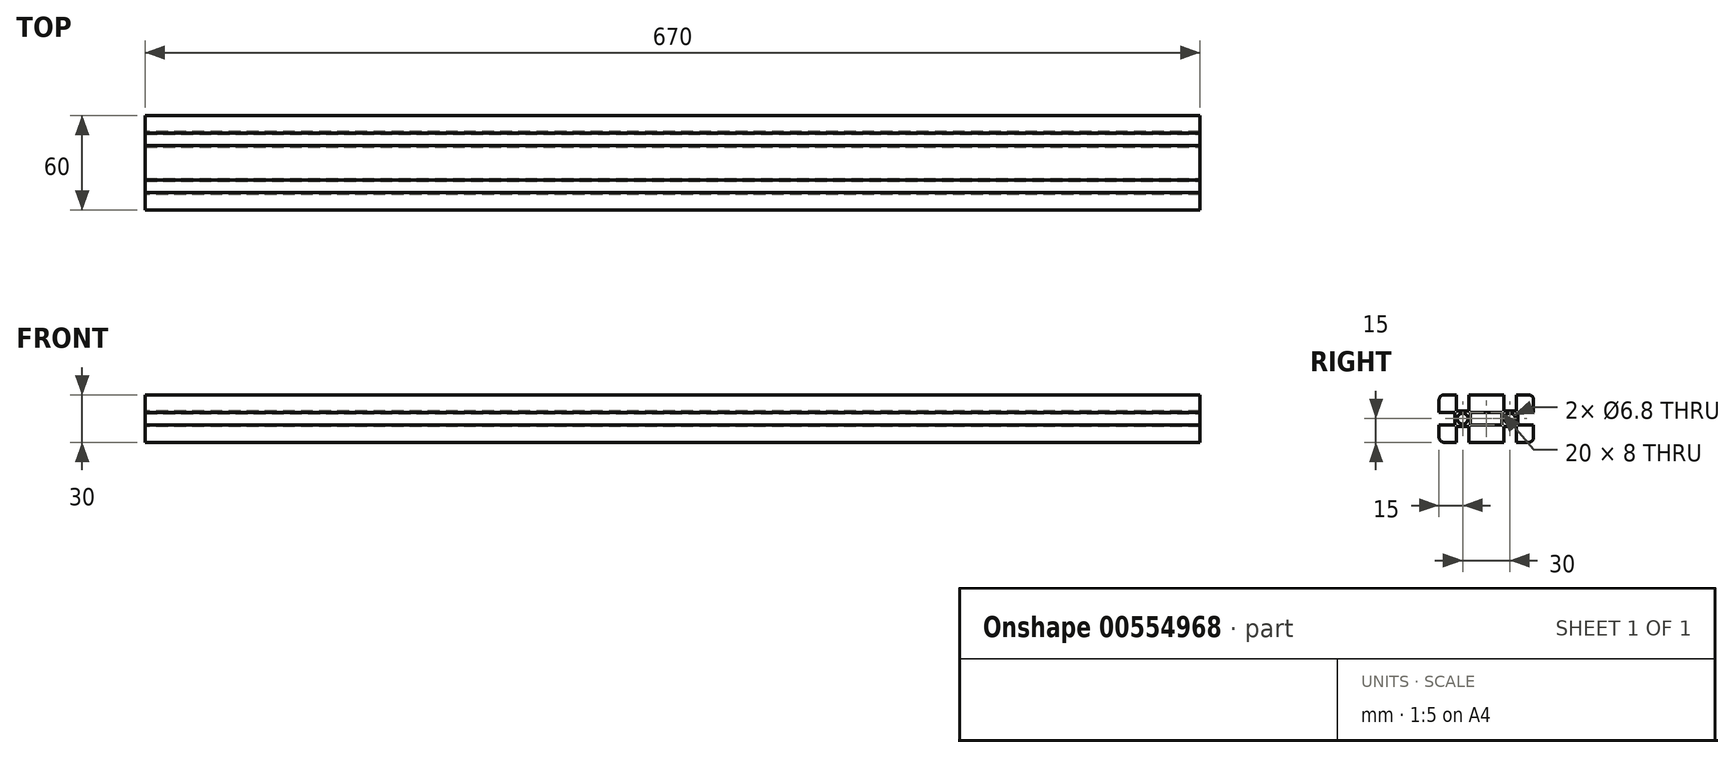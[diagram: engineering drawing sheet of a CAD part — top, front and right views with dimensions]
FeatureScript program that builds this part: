
annotation { "Feature Type Name" : "Feature", "Feature Type Description" : "" }
export const myFeature = defineFeature(function(context is Context, id is Id, definition is map)
    precondition{}
    {
        {
            var Q0;
            Q0=qCreatedBy(makeId("Right.planeOp"),FACE);
            var sketch = newSketch(context, id + "F0", { "sketchPlane" : qUnion([Q0])});
            skLineSegment(sketch, "E0.bottom", {"start": v(30, 15) * mm, "end": v(19, 15) * mm});
            skLineSegment(sketch, "E0.top", {"start": v(30, -15) * mm, "end": v(19, -15) * mm});
            skLineSegment(sketch, "E0.left", {"start": v(30, 15) * mm, "end": v(30, 4) * mm});
            skLineSegment(sketch, "E0.right", {"start": v(-30, 15) * mm, "end": v(-30, 4) * mm});
            skPoint(sketch, "E0.middle", {"position": v(0, 0) * mm});
            skLineSegment(sketch, "E1", {"start": v(-30, 4) * mm, "end": v(-20, 4) * mm});
            skLineSegment(sketch, "E2", {"start": v(-20, 4) * mm, "end": v(-20, -4) * mm});
            skLineSegment(sketch, "E3", {"start": v(-20, -4) * mm, "end": v(-30, -4) * mm});
            skLineSegment(sketch, "E4", {"start": v(-19, 15) * mm, "end": v(-19, 5) * mm});
            skLineSegment(sketch, "E5", {"start": v(-19, 5) * mm, "end": v(-11, 5) * mm});
            skLineSegment(sketch, "E6", {"start": v(-11, 5) * mm, "end": v(-11, 15) * mm});
            skLineSegment(sketch, "E7", {"start": v(-19, -15) * mm, "end": v(-19, -5) * mm});
            skLineSegment(sketch, "E8", {"start": v(-19, -5) * mm, "end": v(-11, -5) * mm});
            skLineSegment(sketch, "E9", {"start": v(-11, -5) * mm, "end": v(-11, -15) * mm});
            skLineSegment(sketch, "E10.MirrorCS", {"start": v(11, 5) * mm, "end": v(11, 15) * mm});
            skLineSegment(sketch, "E11.MirrorCS", {"start": v(20, 4) * mm, "end": v(20, -4) * mm});
            skLineSegment(sketch, "E12.MirrorCS", {"start": v(19, -5) * mm, "end": v(11, -5) * mm});
            skLineSegment(sketch, "E13.MirrorCS", {"start": v(11, -5) * mm, "end": v(11, -15) * mm});
            skLineSegment(sketch, "E14.MirrorCS", {"start": v(19, -15) * mm, "end": v(19, -5) * mm});
            skLineSegment(sketch, "E15.MirrorCS", {"start": v(20, -4) * mm, "end": v(30, -4) * mm});
            skLineSegment(sketch, "E16.MirrorCS", {"start": v(30, 4) * mm, "end": v(20, 4) * mm});
            skLineSegment(sketch, "E17.MirrorCS", {"start": v(19, 5) * mm, "end": v(11, 5) * mm});
            skLineSegment(sketch, "E18.MirrorCS", {"start": v(19, 15) * mm, "end": v(19, 5) * mm});
            skLineSegment(sketch, "E19.trimOffspring", {"start": v(-19, 15) * mm, "end": v(-30, 15) * mm});
            skLineSegment(sketch, "E20.trimOffspring", {"start": v(-30, -4) * mm, "end": v(-30, -15) * mm});
            skLineSegment(sketch, "E21.trimOffspring", {"start": v(-19, -15) * mm, "end": v(-30, -15) * mm});
            skLineSegment(sketch, "E22.trimOffspring", {"start": v(30, -4) * mm, "end": v(30, -15) * mm});
            skLineSegment(sketch, "E23.trimOffspring", {"start": v(11, 15) * mm, "end": v(-11, 15) * mm});
            skLineSegment(sketch, "E24.trimOffspring", {"start": v(11, -15) * mm, "end": v(-11, -15) * mm});
            skSolve(sketch);
        }
        {
            var Q0;
            Q0 = qSketchRegion(id + "F0", true);
            extrude(context, id + "F1", {"entities" : qUnion([Q0]), "endBound" : BoundingType.SYMMETRIC, "depth" : 670 * mm, "offsetDistance" : 25 * mm});
        }
        {
            var Q0;
            Q0=makeQuery(id+"F1.opExtrude","CAP_FACE",FACE,{"disambiguationData":[OSD([sQuery(id+"F0.wireOp",EDGE,"E0.bottom"),sQuery(id+"F0.wireOp",EDGE,"E0.top"),sQuery(id+"F0.wireOp",EDGE,"E0.left"),sQuery(id+"F0.wireOp",EDGE,"E0.right"),sQuery(id+"F0.wireOp",EDGE,"E1"),sQuery(id+"F0.wireOp",EDGE,"E2"),sQuery(id+"F0.wireOp",EDGE,"E3"),sQuery(id+"F0.wireOp",EDGE,"E4"),sQuery(id+"F0.wireOp",EDGE,"E5"),sQuery(id+"F0.wireOp",EDGE,"E6"),sQuery(id+"F0.wireOp",EDGE,"E7"),sQuery(id+"F0.wireOp",EDGE,"E8"),sQuery(id+"F0.wireOp",EDGE,"E9"),sQuery(id+"F0.wireOp",EDGE,"E10.MirrorCS"),sQuery(id+"F0.wireOp",EDGE,"E11.MirrorCS"),sQuery(id+"F0.wireOp",EDGE,"E12.MirrorCS"),sQuery(id+"F0.wireOp",EDGE,"E13.MirrorCS"),sQuery(id+"F0.wireOp",EDGE,"E14.MirrorCS"),sQuery(id+"F0.wireOp",EDGE,"E15.MirrorCS"),sQuery(id+"F0.wireOp",EDGE,"E16.MirrorCS"),sQuery(id+"F0.wireOp",EDGE,"E17.MirrorCS"),sQuery(id+"F0.wireOp",EDGE,"E18.MirrorCS"),sQuery(id+"F0.wireOp",EDGE,"E19.trimOffspring"),sQuery(id+"F0.wireOp",EDGE,"E20.trimOffspring"),sQuery(id+"F0.wireOp",EDGE,"E21.trimOffspring"),sQuery(id+"F0.wireOp",EDGE,"E22.trimOffspring"),sQuery(id+"F0.wireOp",EDGE,"E23.trimOffspring"),sQuery(id+"F0.wireOp",EDGE,"E24.trimOffspring")])],"isStart":false});
            var sketch = newSketch(context, id + "F2", { "sketchPlane" : qUnion([Q0])});
            skLineSegment(sketch, "E25.bottom", {"start": v(10, 4) * mm, "end": v(-10, 4) * mm});
            skLineSegment(sketch, "E25.top", {"start": v(10, -4) * mm, "end": v(-10, -4) * mm});
            skLineSegment(sketch, "E25.left", {"start": v(10, 4) * mm, "end": v(10, -4) * mm});
            skLineSegment(sketch, "E25.right", {"start": v(-10, 4) * mm, "end": v(-10, -4) * mm});
            skPoint(sketch, "E25.middle", {"position": v(0, 0) * mm});
            skCircle(sketch, "E26", {"center": v(-15, 0) * mm, "radius": 3.4 * mm});
            skCircle(sketch, "E27", {"center": v(15, 0) * mm, "radius": 3.4 * mm});
            skSolve(sketch);
        }
        {
            var Q0;
            Q0 = qSketchRegion(id + "F2", true);
            extrude(context, id + "F3", {"entities" : qUnion([Q0]), "operationType" : NewBodyOperationType.REMOVE, "oppositeDirection" : true, "depth" : 670 * mm, "offsetDistance" : 25 * mm});
        }
        {
            var Q0;
            Q0=makeQuery(id+"F1.opExtrude","SWEPT_EDGE",EDGE,{"disambiguationData":[OSD([sQuery(id+"F0.wireOp",EDGE,"E0.right"),sQuery(id+"F0.wireOp",EDGE,"E19.trimOffspring")])]});
            var Q1;
            Q1=makeQuery(id+"F1.opExtrude","SWEPT_EDGE",EDGE,{"disambiguationData":[OSD([sQuery(id+"F0.wireOp",EDGE,"E20.trimOffspring"),sQuery(id+"F0.wireOp",EDGE,"E21.trimOffspring")])]});
            var Q2;
            Q2=makeQuery(id+"F1.opExtrude","SWEPT_EDGE",EDGE,{"disambiguationData":[OSD([sQuery(id+"F0.wireOp",EDGE,"E0.bottom"),sQuery(id+"F0.wireOp",EDGE,"E0.left")])]});
            var Q3;
            Q3=makeQuery(id+"F1.opExtrude","SWEPT_EDGE",EDGE,{"disambiguationData":[OSD([sQuery(id+"F0.wireOp",EDGE,"E0.top"),sQuery(id+"F0.wireOp",EDGE,"E22.trimOffspring")])]});
            fillet(context, id + "F4", {"entities" : qUnion([Q0, Q1, Q2, Q3]), "radius" : 3 * mm, "tangentPropagation" : true, "allowEdgeOverflow" : false});
        }
    });
